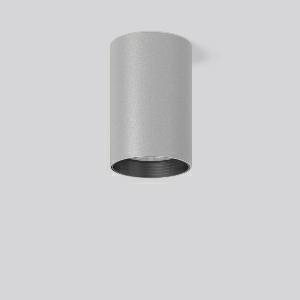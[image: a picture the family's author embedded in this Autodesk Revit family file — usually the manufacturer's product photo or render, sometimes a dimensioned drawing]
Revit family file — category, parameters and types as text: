
# Revit family: heledon_maxi_a_931227_004_2_7525
name_source: partatom
category: Lighting Fixtures
units: mm (PartAtom-declared; Revit-internal decimal feet)

## family parameters
Cut with Voids When Loaded = No
Host = Face
Light Source = No
Part Type = Normal
Room Calculation Point = No
Round Connector Dimension = Use Diameter
Shared = No

## types (1)
- HELEDON maxi A (1 x LED Modul 927, 3500 lm, 2700)
    Apparent Load = 35 VA
    Approval mark = CE
    CIE Flux Codes = 97 100 100 100 100
    Color Rendering = 92
    Color Temperature = 2700
    Default Elevation = 1800 mm
    Description = Series: HELEDON maxi
Cylindrical surface-mounted downlight. Housing: die-cast aluminium, powder-coated. Internal ceiling frame polycarbonate with bayonet mounting. Black plastic ring and recessed LED to prevent glare from the side. Optical assembly with lens made of plastic (polycarbonate) for the best homogeneous light distribution - can be changed without tools. Best colour rendering index Ra>90. Suitable for Ceiling mounting. Easy installation with a separate ceiling frame with bayonet mounting and plug connection. Driver integrated. Connected via plug-in connector. High quality converter without flickering and stroboscopic effect. The following accessories can be mounted without use of tools: interchangeable lenses, decorative glasses, honeycomb louvre, clear and frosted diffusers, white interchangeable plastic ring. 
Colour: silver
Diameter: 123 mm
Height: 183 mm
Lamp: LED
Socket: without socket
Colour temperature: 2700K
Colour rendering index (CRI): 92
System power: 35 W
Rated luminous flux: 3500 lm
Luminous efficiency: 100 lm/W
Control gear: Regulated power supply
Protection class: I
Type of protection: IP 20
    Height = 183 mm
    Lamp = 1 x LED Modul 927
    Lamp Light Flux = 3500 lm
    Lamp count = 1
    Length = 123 mm
    Lifetime = 50000 h
    Luminous efficacy = 100 lm/W
    Manufacturer = RZB
    ModVariant = No
    Model = 931227.004.2
    Mounting Place = Ceiling
    Mounting Type = Surface mounted
    Number of Poles = 1
    OnlyDefault = Yes
    Power Factor = 1
    Product Name = HELEDON maxi A
    Product group = Surface mounted downlights
    ProductGroupID = 302
    Protection Class = Protection class I
    Protection Degree = IP 20
    RLX_Detail_Level = 1
    RLX_Emergency_Light_Flux = 0 lm
    RLX_Emergency_Type = 0
    RLX_Emergency_Type_DB = No
    RlxData = <blob elided: 98833 chars, md5=580d5f6d>
    Socket = socket
    Standby Power = 0 W
    System Light Flux = 3500 lm
    System Power = 35 W
    Type Comments = Product without accessories
    Type Image = 931193.004.jpg
    URL = http://relux.com
    VarID = ---
    Voltage = 230 V
    Voltage Range = 220-240 V
    Weight = 0.00 kg
    Width = 0 mm  [stored 0 ft]

note: [stored X ft] marks values corroborated as IEEE doubles in the binary element streams (Revit-internal decimal feet)

## geometry (parser evidence)
native form markers: Blend x4, Sweep x10
no freeform markers — native parametric forms only
